# Revit family: DF_ЗажимЗаземлпения_Стержень_Полоса_90530_90540_EZETEK
name_source: partatom
category: Соединительные детали воздуховодов
revit_build: Autodesk Revit 2017 (Build: 20170118_1100(x64)
units: mm (PartAtom-declared; Revit-internal decimal feet)

## family parameters
Всегда вертикально = Да
На основе рабочей плоскости = Нет
Общий = Нет
При загрузке вырезать с полостями = Нет
Размер круглого соединителя = Использовать радиус
Тип детали = Крестовина

## types (2) — shared parameters
ADSK_Версия Revit = 2017
ADSK_Единица измерения = Неспецифицируемое
ADSK_Завод-изготовитель = Неспецифицируемое
ADSK_Код изделия = Неспецифицируемое
ADSK_Марка = Неспецифицируемое
ADSK_Масса_Текст = Неспецифицируемое
ADSK_Наименование = Неспецифицируемое
ADSK_Обозначение = Неспецифицируемое
URL = https://ezetek.ru
Группа модели = Зажимы заземления
Изготовитель = Ezetek
Описание = Зажим используются для соединения стержня заземления с прутком, либо полосой Т-образным либо параллельным способом. Зажим стягивается при помощи четырех шестигранных болтов с гайками с резьбой М8.
Угол = 90.00°
zero-valued in all types: ADSK_Количество, ADSK_Масса

## per-type parameters (varying)
| type | ADSK_Материал | Тип |
| ЗажимЗаземлпения_Полоса_Пруток_Оцинкованный_90530 | BIMLIB_Сталь_Оцинкованная_EZETEK | FA_ЗажимЗаземлпения_Стержень_Полоса-Пруток_90530_90540_EZETEK : ЗажимЗаземлпения_Стержень_Полоса-Пруток_Оцинкованный_90540 |
| ЗажимЗаземлпения_Стержень_Полоса_Оцинкованный_90540 | BIMLIB_Латунь_EZETEK | FA_ЗажимЗаземлпения_Стержень_Полоса-Пруток_90530_90540_EZETEK : ЗажимЗаземлпения_Стержень_Полоса-Пруток_Латунь_90530 |
